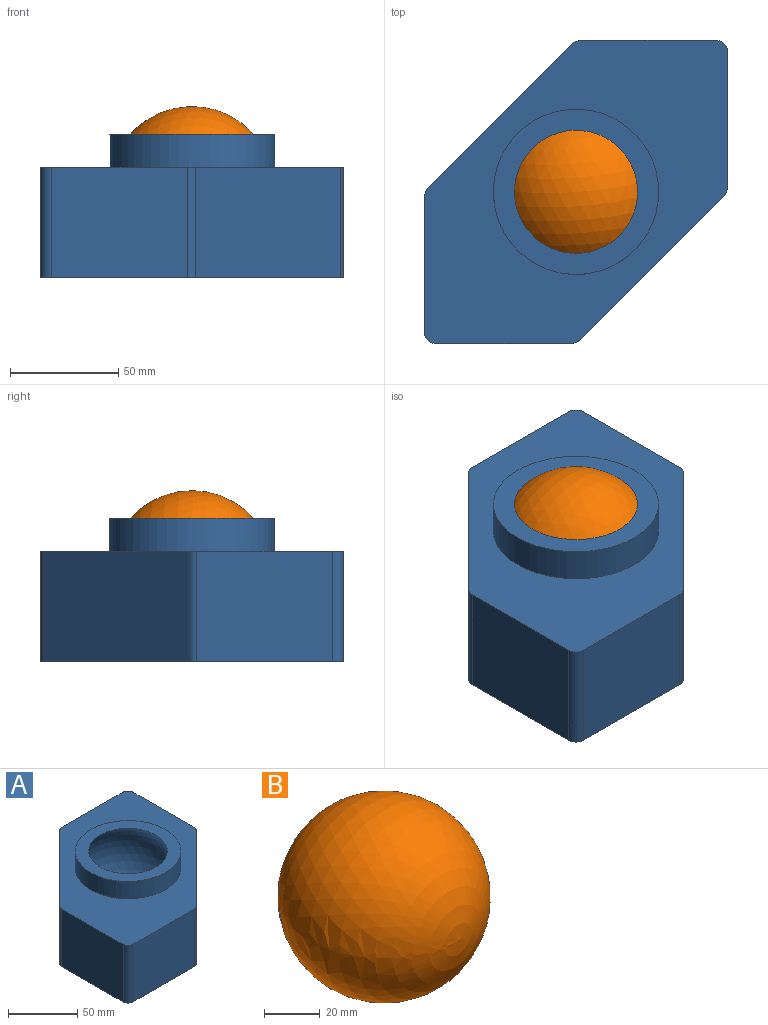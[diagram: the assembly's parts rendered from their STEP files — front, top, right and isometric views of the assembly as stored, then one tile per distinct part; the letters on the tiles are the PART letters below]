
ASSEMBLY  parts=2 mates=1
PART A: 17 faces, bbox 139.7x139.7x66 mm
  f0: plane 62.67x50.8mm, normal (0,-1,0), area 3183.4mm2, adj f6,f7,f11,f16
  f1: plane 66.87x66.87mm, normal (0.71,-0.71,0), area 4804.4mm2, adj f6,f7,f11,f12
  f2: plane 62.67x50.8mm, normal (1,0,0), area 3183.4mm2, adj f6,f7,f12,f13
  f3: plane 62.67x50.8mm, normal (0,1,0), area 3183.4mm2, adj f6,f7,f13,f14
  f4: plane 66.87x66.87mm, normal (-0.71,0.71,0), area 4804.4mm2, adj f6,f7,f14,f15
  f5: plane 62.67x50.8mm, normal (-1,0,0), area 3183.4mm2, adj f6,f7,f15,f16
  f6: plane 139.7x139.7mm, normal (0,0,-1), area 14623.8mm2, adj f0,f1,f2,f3,f4,f5,f11,f12
  f7: plane 139.7x139.7mm, normal (0,0,1), area 10063.4mm2, adj f0,f1,f2,f3,f4,f5,f8,f11
  f8: cylinder r=38.1mm len=76.2mm, axis (0,0,-1), area 3648.3mm2, adj f7,f9
  f9: plane 76.2x76.2mm, normal (0,0,1), area 2026.8mm2, adj f8,f10
  f10: sphere r=38.1mm, area 15201.2mm2, adj f9
  f11: cylinder r=5.08mm len=50.8mm, axis (0,0,-1), area 202.7mm2, adj f0,f1,f6,f7
  f12: cylinder r=5.08mm len=50.8mm, axis (0,0,-1), area 202.7mm2, adj f1,f2,f6,f7
  f13: cylinder r=5.08mm len=50.8mm, axis (0,0,-1), area 405.4mm2, adj f2,f3,f6,f7
  f14: cylinder r=5.08mm len=50.8mm, axis (0,0,1), area 202.7mm2, adj f3,f4,f6,f7
  f15: cylinder r=5.08mm len=50.8mm, axis (0,0,1), area 202.7mm2, adj f4,f5,f6,f7
  f16: cylinder r=5.08mm len=50.8mm, axis (0,0,-1), area 405.4mm2, adj f0,f5,f6,f7
PART B: 1 faces, bbox 76.2x76.2x76.2 mm
  f0: sphere r=38.1mm, area 18241.5mm2
PLACE A t=(-38.24,21.81,33.88)mm fixed
PLACE B rot(axis=(0.32,-0.95,0.03),34.1deg) t=(-154.85,26.74,-49.55)mm
MATE ball B.f0 <-> A.f8  axis (-0.53,-0.19,0.83) through (-38.24,21.81,23.72)mm
